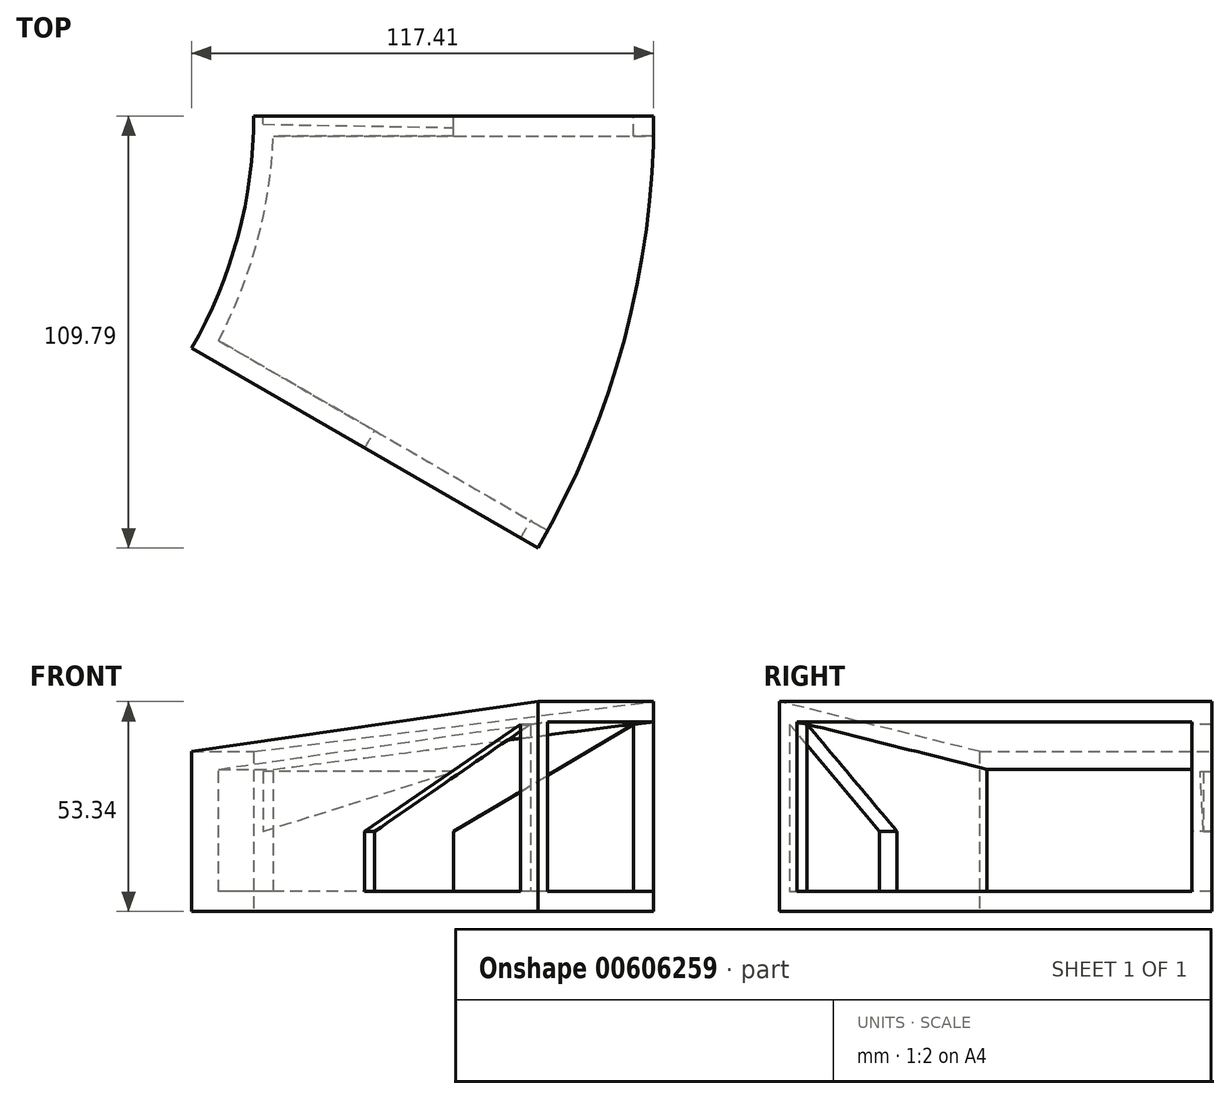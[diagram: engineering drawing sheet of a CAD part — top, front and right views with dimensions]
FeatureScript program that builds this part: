
annotation { "Feature Type Name" : "Feature", "Feature Type Description" : "" }
export const myFeature = defineFeature(function(context is Context, id is Id, definition is map)
    precondition{}
    {
        {
            var Q0;
            Q0=qCreatedBy(makeId("Front.planeOp"),FACE);
            var sketch = newSketch(context, id + "F0", { "sketchPlane" : qUnion([Q0])});
            skLineSegment(sketch, "E0.bottom", {"start": v(50.8, 20.32) * mm, "end": v(-50.8, 20.32) * mm, "construction": true});
            skLineSegment(sketch, "E0.top", {"start": v(50.8, -20.32) * mm, "end": v(-50.8, -20.32) * mm});
            skLineSegment(sketch, "E0.left", {"start": v(50.8, 20.32) * mm, "end": v(50.8, -20.32) * mm});
            skLineSegment(sketch, "E0.right", {"start": v(-50.8, 20.32) * mm, "end": v(-50.8, -20.32) * mm});
            skPoint(sketch, "E0.middle", {"position": v(0, 0) * mm});
            skLineSegment(sketch, "E1", {"start": v(-50.8, 20.32) * mm, "end": v(50.8, 33.02) * mm});
            skLineSegment(sketch, "E2", {"start": v(50.8, 33.02) * mm, "end": v(50.8, 20.32) * mm});
            skLineSegment(sketch, "E3", {"start": v(-168.78, 401.1) * mm, "end": v(-168.78, -106.9) * mm, "construction": true});
            skSolve(sketch);
        }
        {
            var Q0;
            Q0 = qSketchRegion(id + "F0", true);
            var Q1;
            Q1=sQuery(id+"F0.wireOp",EDGE,"E3");
            revolve(context, id + "F1", {"surfaceOperationType" : NewSurfaceOperationType.NEW, "entities" : qUnion([Q0]), "axis" : qUnion([Q1]), "revolveType" : RevolveType.ONE_DIRECTION, "angle" : 30 * degree});
        }
        {
            var Q0;
            Q0=makeQuery(id+"F1.opRevolve","SWEPT_FACE",FACE,{"disambiguationData":[OSD([sQuery(id+"F0.wireOp",EDGE,"E0.left"),sQuery(id+"F0.wireOp",EDGE,"E2")])]});
            shell(context, id + "F2", {"entities" : qUnion([Q0]), "thickness" : 5.08 * mm});
        }
        {
            var Q0;
            Q0=makeQuery(id+"F1.opRevolve","CAP_FACE",FACE,{"disambiguationData":[OSD([sQuery(id+"F0.wireOp",EDGE,"E0.top"),sQuery(id+"F0.wireOp",EDGE,"E0.left"),sQuery(id+"F0.wireOp",EDGE,"E0.right"),sQuery(id+"F0.wireOp",EDGE,"E1"),sQuery(id+"F0.wireOp",EDGE,"E2")])],"isStart":true});
            var sketch = newSketch(context, id + "F3", { "sketchPlane" : qUnion([Q0])});
            skLineSegment(sketch, "E4", {"start": v(-45.72, 27.27) * mm, "end": v(-45.72, -15.24) * mm});
            skLineSegment(sketch, "E5", {"start": v(-45.72, -15.24) * mm, "end": v(0, -15.24) * mm});
            skLineSegment(sketch, "E6", {"start": v(0, -15.24) * mm, "end": v(0, 0) * mm});
            skLineSegment(sketch, "E7", {"start": v(0, 0) * mm, "end": v(-45.72, 27.27) * mm});
            skPoint(sketch, "E8", {"position": v(0, -7.62) * mm});
            skSolve(sketch);
        }
        {
            var Q0;
            Q0 = qSketchRegion(id + "F3", true);
            var Q1;
            Q1=sQuery(id+"F0.wireOp",EDGE,"E3");
            revolve(context, id + "F4", {"operationType" : NewBodyOperationType.REMOVE, "surfaceOperationType" : NewSurfaceOperationType.NEW, "entities" : qUnion([Q0]), "axis" : qUnion([Q1]), "revolveType" : RevolveType.FULL, "oppositeDirection" : true});
        }
        {
            var Q0;
            Q0=makeQuery(id+"F0.imprint","IMPRINT",FACE,{"disambiguationData":[TD([[makeQuery(id+"F0.imprint","IMPRINT",EDGE,{"derivedFrom":sQuery(id+"F0.wireOp",EDGE,"E0.top")}),-1.0]])]});
            var sketch = newSketch(context, id + "F5", { "sketchPlane" : qUnion([Q0])});
            skLineSegment(sketch, "E9", {"start": v(-48.46, 0) * mm, "end": v(0, 15.24) * mm});
            skLineSegment(sketch, "E10", {"start": v(0, 15.24) * mm, "end": v(-48.46, 15.24) * mm});
            skLineSegment(sketch, "E11", {"start": v(-48.46, 15.24) * mm, "end": v(-48.46, 0) * mm});
            skSolve(sketch);
        }
        {
            var Q0;
            Q0 = qSketchRegion(id + "F5", true);
            var Q1;
            Q1=sQuery(id+"F0.wireOp",EDGE,"E3");
            revolve(context, id + "F6", {"operationType" : NewBodyOperationType.REMOVE, "surfaceOperationType" : NewSurfaceOperationType.NEW, "entities" : qUnion([Q0]), "axis" : qUnion([Q1]), "revolveType" : RevolveType.ONE_DIRECTION, "angle" : 1 * degree});
        }
    });
